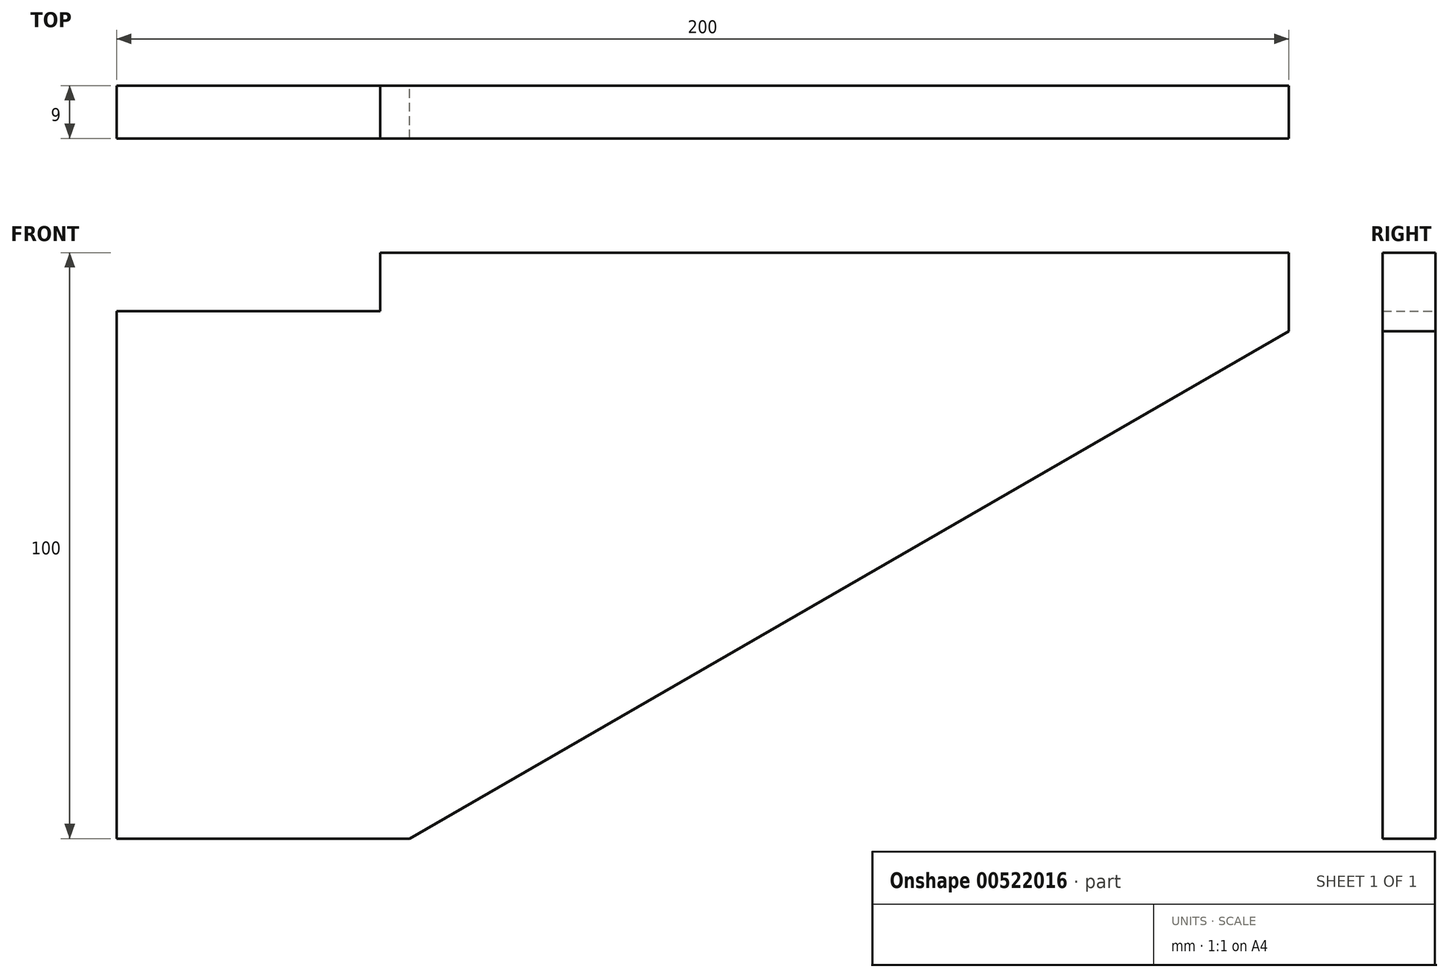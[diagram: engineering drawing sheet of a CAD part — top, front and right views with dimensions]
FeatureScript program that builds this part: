
annotation { "Feature Type Name" : "Feature", "Feature Type Description" : "" }
export const myFeature = defineFeature(function(context is Context, id is Id, definition is map)
    precondition{}
    {
        {
            var Q0;
            Q0=qCreatedBy(makeId("Front.planeOp"),FACE);
            var sketch = newSketch(context, id + "F0", { "sketchPlane" : qUnion([Q0])});
            skLineSegment(sketch, "E0", {"start": v(0, 0) * mm, "end": v(50, 0) * mm});
            skLineSegment(sketch, "E1", {"start": v(50, 0) * mm, "end": v(200, 86.6) * mm});
            skLineSegment(sketch, "E2", {"start": v(200, 86.6) * mm, "end": v(200, 100) * mm});
            skLineSegment(sketch, "E3", {"start": v(200, 100) * mm, "end": v(45, 100) * mm});
            skLineSegment(sketch, "E4", {"start": v(45, 100) * mm, "end": v(45, 90) * mm});
            skLineSegment(sketch, "E5", {"start": v(45, 90) * mm, "end": v(0, 90) * mm});
            skLineSegment(sketch, "E6", {"start": v(0, 90) * mm, "end": v(0, 0) * mm});
            skSolve(sketch);
        }
        {
            var Q0;
            Q0=makeQuery(id+"F0.imprint","IMPRINT",FACE,{"disambiguationData":[TD([[makeQuery(id+"F0.imprint","IMPRINT",EDGE,{"derivedFrom":sQuery(id+"F0.wireOp",EDGE,"E0")}),1.0]])]});
            extrude(context, id + "F1", {"entities" : qUnion([Q0]), "depth" : 9 * mm, "offsetDistance" : 25 * mm});
        }
    });
